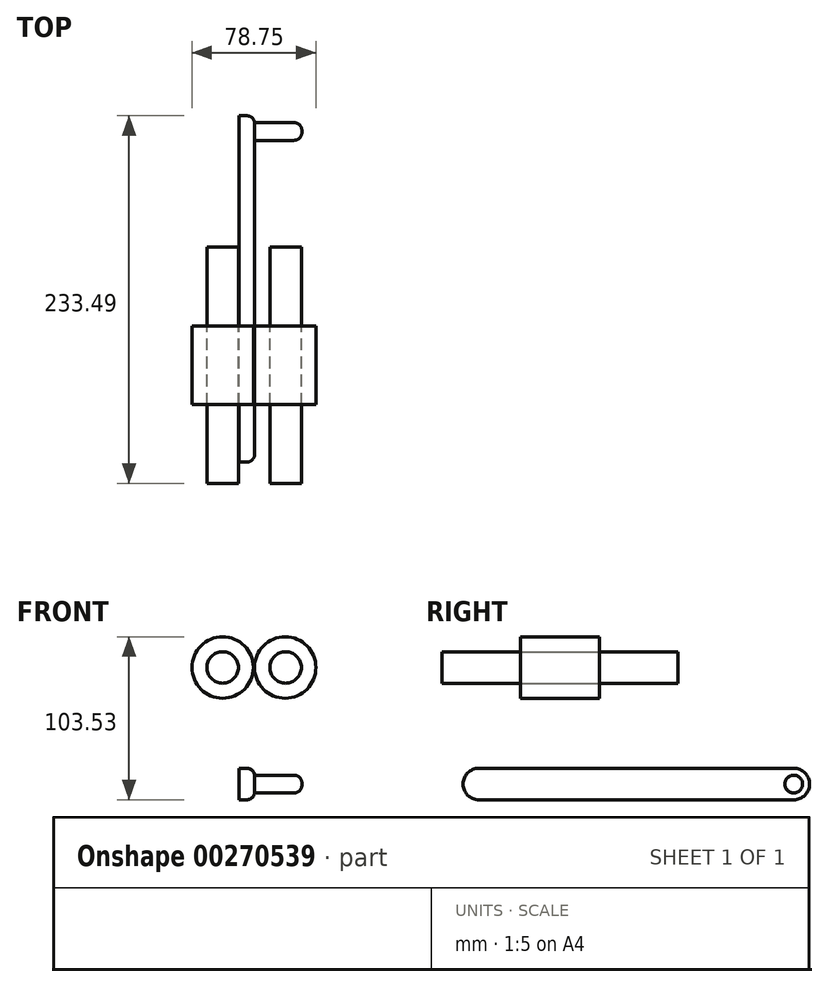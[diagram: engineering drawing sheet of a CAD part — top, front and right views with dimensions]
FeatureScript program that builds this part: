
annotation { "Feature Type Name" : "Feature", "Feature Type Description" : "" }
export const myFeature = defineFeature(function(context is Context, id is Id, definition is map)
    precondition{}
    {
        {
            var Q0;
            Q0=qCreatedBy(makeId("Front.planeOp"),FACE);
            var sketch = newSketch(context, id + "F0", { "sketchPlane" : qUnion([Q0])});
            skCircle(sketch, "E0", {"center": v(29.66, 37.05) * mm, "radius": 10 * mm});
            skCircle(sketch, "E1", {"center": v(-10.34, 37.05) * mm, "radius": 10 * mm});
            skLineSegment(sketch, "E2", {"start": v(-36.98, 37.05) * mm, "end": v(95.8, 37.05) * mm});
            skSolve(sketch);
        }
        {
            var Q0;
            Q0 = qSketchRegion(id + "F0", true);
            extrude(context, id + "F1", {"entities" : qUnion([Q0]), "endBound" : BoundingType.SYMMETRIC, "depth" : 150 * mm});
        }
        {
            var Q0;
            Q0=qCreatedBy(makeId("Front.planeOp"),FACE);
            var sketch = newSketch(context, id + "F2", { "sketchPlane" : qUnion([Q0])});
            skCircle(sketch, "E3", {"center": v(29.41, 37.05) * mm, "radius": 19.5 * mm});
            skCircle(sketch, "E4", {"center": v(-10.34, 37.05) * mm, "radius": 19.5 * mm});
            skSolve(sketch);
        }
        {
            var Q0;
            Q0 = qSketchRegion(id + "F2", true);
            extrude(context, id + "F3", {"entities" : qUnion([Q0]), "endBound" : BoundingType.SYMMETRIC, "depth" : 50 * mm});
        }
        {
            var Q0;
            Q0=qCreatedBy(makeId("Right.planeOp"),FACE);
            var sketch = newSketch(context, id + "F4", { "sketchPlane" : qUnion([Q0])});
            skLineSegment(sketch, "E5", {"start": v(-51.5, -26.98) * mm, "end": v(148.5, -26.98) * mm});
            skLineSegment(sketch, "E6", {"start": v(-51.5, -46.98) * mm, "end": v(148.5, -46.98) * mm});
            skArc(sketch, "E7", {"start": v(148.5, -46.98) * mm, "mid": v(158.5, -36.98) * mm, "end": v(148.5, -26.98) * mm});
            skCircle(sketch, "E8", {"center": v(-51.5, -36.98) * mm, "radius": 10 * mm});
            skCircle(sketch, "E9", {"center": v(148.5, -36.98) * mm, "radius": 5.64 * mm});
            skSolve(sketch);
        }
        {
            var Q0;
            Q0=makeQuery(id+"F4.imprint","IMPRINT",FACE,{"disambiguationData":[TD([[makeQuery(id+"F4.imprint","IMPRINT",EDGE,{"derivedFrom":sQuery(id+"F4.wireOp",EDGE,"E9")}),1.0]])]});
            extrude(context, id + "F5", {"entities" : qUnion([Q0]), "depth" : 40 * mm});
        }
        {
            var Q0;
            Q0 = qSketchRegion(id + "F4", true);
            extrude(context, id + "F6", {"entities" : qUnion([Q0]), "operationType" : NewBodyOperationType.ADD, "depth" : 10 * mm});
        }
        {
            var Q0;
            Q0=makeQuery(id+"F6.opExtrude","CAP_EDGE",EDGE,{"disambiguationData":[OSD([sQuery(id+"F4.wireOp",EDGE,"E6")])],"isStart":false});
            var Q1;
            Q1=makeQuery(id+"F5.opExtrude","CAP_EDGE",EDGE,{"disambiguationData":[OSD([sQuery(id+"F4.wireOp",EDGE,"E9")])],"isStart":false});
            fillet(context, id + "F7", {"entities" : qUnion([Q0, Q1]), "radius" : 5 * mm, "tangentPropagation" : true, "allowEdgeOverflow" : false});
        }
    });
